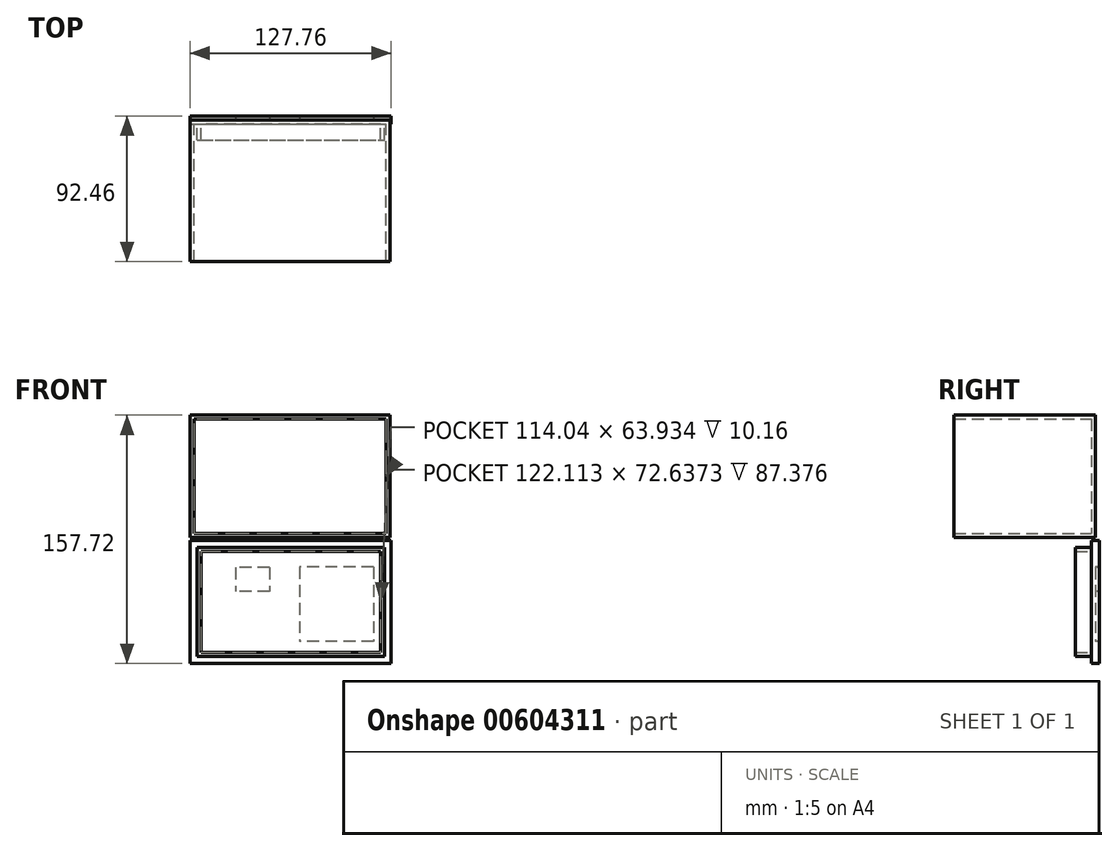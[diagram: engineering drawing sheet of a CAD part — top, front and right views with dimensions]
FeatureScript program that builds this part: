
annotation { "Feature Type Name" : "Feature", "Feature Type Description" : "" }
export const myFeature = defineFeature(function(context is Context, id is Id, definition is map)
    precondition{}
    {
        {
            var Q0;
            Q0=qCreatedBy(makeId("Front.planeOp"),FACE);
            var sketch = newSketch(context, id + "F0", { "sketchPlane" : qUnion([Q0])});
            skLineSegment(sketch, "E0.bottom", {"start": v(-147.35, 70.95) * mm, "end": v(-20.16, 70.95) * mm});
            skLineSegment(sketch, "E0.top", {"start": v(-147.35, -6.76) * mm, "end": v(-20.16, -6.76) * mm});
            skLineSegment(sketch, "E0.left", {"start": v(-147.35, 70.95) * mm, "end": v(-147.35, -6.76) * mm});
            skLineSegment(sketch, "E0.right", {"start": v(-20.16, 70.95) * mm, "end": v(-20.16, -6.76) * mm});
            skSolve(sketch);
        }
        {
            var Q0;
            Q0=makeQuery(id+"F0.imprint","IMPRINT",FACE,{"disambiguationData":[TD([[makeQuery(id+"F0.imprint","IMPRINT",EDGE,{"derivedFrom":sQuery(id+"F0.wireOp",EDGE,"E0.bottom")}),-1.0]])]});
            extrude(context, id + "F1", {"entities" : qUnion([Q0]), "depth" : 89.92 * mm, "offsetDistance" : 25.4 * mm});
        }
        {
            var Q0;
            Q0=makeQuery(id+"F1.opExtrude","CAP_FACE",FACE,{"disambiguationData":[OSD([sQuery(id+"F0.wireOp",EDGE,"E0.bottom"),sQuery(id+"F0.wireOp",EDGE,"E0.top"),sQuery(id+"F0.wireOp",EDGE,"E0.left"),sQuery(id+"F0.wireOp",EDGE,"E0.right")])],"isStart":false});
            shell(context, id + "F2", {"entities" : qUnion([Q0]), "thickness" : 2.54 * mm});
        }
        {
            var Q0;
            Q0=qCreatedBy(makeId("Front.planeOp"),FACE);
            var sketch = newSketch(context, id + "F3", { "sketchPlane" : qUnion([Q0])});
            skLineSegment(sketch, "E1.bottom", {"start": v(-147.14, -8.8) * mm, "end": v(-19.6, -8.8) * mm});
            skLineSegment(sketch, "E1.top", {"start": v(-147.14, -86.77) * mm, "end": v(-19.6, -86.77) * mm});
            skLineSegment(sketch, "E1.left", {"start": v(-147.14, -8.8) * mm, "end": v(-147.14, -86.77) * mm});
            skLineSegment(sketch, "E1.right", {"start": v(-19.6, -8.8) * mm, "end": v(-19.6, -86.77) * mm});
            skSolve(sketch);
        }
        {
            var Q0;
            Q0=makeQuery(id+"F3.imprint","IMPRINT",FACE,{"disambiguationData":[TD([[makeQuery(id+"F3.imprint","IMPRINT",EDGE,{"derivedFrom":sQuery(id+"F3.wireOp",EDGE,"E1.bottom")}),-1.0]])]});
            extrude(context, id + "F4", {"entities" : qUnion([Q0]), "depth" : 2.54 * mm, "offsetDistance" : 25.4 * mm});
        }
        {
            var Q0;
            Q0=makeQuery(id+"F4.opExtrude","CAP_FACE",FACE,{"disambiguationData":[OSD([sQuery(id+"F3.wireOp",EDGE,"E1.bottom"),sQuery(id+"F3.wireOp",EDGE,"E1.top"),sQuery(id+"F3.wireOp",EDGE,"E1.left"),sQuery(id+"F3.wireOp",EDGE,"E1.right")])],"isStart":false});
            var sketch = newSketch(context, id + "F5", { "sketchPlane" : qUnion([Q0])});
            skLineSegment(sketch, "E2.bottom", {"start": v(-142.77, -13.16) * mm, "end": v(-23.65, -13.16) * mm});
            skLineSegment(sketch, "E2.top", {"start": v(-142.77, -82.18) * mm, "end": v(-23.65, -82.18) * mm});
            skLineSegment(sketch, "E2.left", {"start": v(-142.77, -13.16) * mm, "end": v(-142.77, -82.18) * mm});
            skLineSegment(sketch, "E2.right", {"start": v(-23.65, -13.16) * mm, "end": v(-23.65, -82.18) * mm});
            skSolve(sketch);
        }
        {
            var Q0;
            Q0=makeQuery(id+"F5.imprint","IMPRINT",FACE,{"disambiguationData":[TD([[makeQuery(id+"F5.imprint","IMPRINT",EDGE,{"derivedFrom":sQuery(id+"F5.wireOp",EDGE,"E2.bottom")}),-1.0]])]});
            extrude(context, id + "F6", {"entities" : qUnion([Q0]), "operationType" : NewBodyOperationType.ADD, "depth" : 10.16 * mm, "offsetDistance" : 25.4 * mm});
        }
        {
            var Q0;
            Q0=makeQuery(id+"F4.opExtrude","CAP_FACE",FACE,{"disambiguationData":[OSD([sQuery(id+"F3.wireOp",EDGE,"E1.bottom"),sQuery(id+"F3.wireOp",EDGE,"E1.top"),sQuery(id+"F3.wireOp",EDGE,"E1.left"),sQuery(id+"F3.wireOp",EDGE,"E1.right")])],"isStart":true});
            var sketch = newSketch(context, id + "F7", { "sketchPlane" : qUnion([Q0])});
            skLineSegment(sketch, "E3.bottom", {"start": v(30.85, -25.45) * mm, "end": v(77.8, -25.45) * mm});
            skLineSegment(sketch, "E3.top", {"start": v(30.85, -72.72) * mm, "end": v(77.8, -72.72) * mm});
            skLineSegment(sketch, "E3.left", {"start": v(30.85, -25.45) * mm, "end": v(30.85, -72.72) * mm});
            skLineSegment(sketch, "E3.right", {"start": v(77.8, -25.45) * mm, "end": v(77.8, -72.72) * mm});
            skSolve(sketch);
        }
        {
            var Q0;
            Q0=makeQuery(id+"F7.imprint","IMPRINT",FACE,{"disambiguationData":[TD([[makeQuery(id+"F7.imprint","IMPRINT",EDGE,{"derivedFrom":sQuery(id+"F7.wireOp",EDGE,"E3.bottom")}),1.0]])]});
            var sketch = newSketch(context, id + "F8", { "sketchPlane" : qUnion([Q0])});
            skLineSegment(sketch, "E4.bottom", {"start": v(96.86, -25.9) * mm, "end": v(118.5, -25.9) * mm});
            skLineSegment(sketch, "E4.top", {"start": v(96.86, -41.15) * mm, "end": v(118.5, -41.15) * mm});
            skLineSegment(sketch, "E4.left", {"start": v(96.86, -25.9) * mm, "end": v(96.86, -41.15) * mm});
            skLineSegment(sketch, "E4.right", {"start": v(118.5, -25.9) * mm, "end": v(118.5, -41.15) * mm});
            skSolve(sketch);
        }
        {
            var Q0;
            Q0=makeQuery(id+"F6.opExtrude","CAP_FACE",FACE,{"disambiguationData":[OSD([sQuery(id+"F5.wireOp",EDGE,"E2.bottom"),sQuery(id+"F5.wireOp",EDGE,"E2.top"),sQuery(id+"F5.wireOp",EDGE,"E2.left"),sQuery(id+"F5.wireOp",EDGE,"E2.right")])],"isStart":false});
            shell(context, id + "F9", {"entities" : qUnion([Q0]), "thickness" : 2.54 * mm});
        }
        {
            var Q0;
            Q0=makeQuery(id+"F8.imprint","IMPRINT",FACE,{"disambiguationData":[TD([[makeQuery(id+"F8.imprint","IMPRINT",EDGE,{"derivedFrom":sQuery(id+"F8.wireOp",EDGE,"E4.bottom")}),1.0]])]});
            extrude(context, id + "F10", {"entities" : qUnion([Q0]), "operationType" : NewBodyOperationType.ADD, "depth" : 2.54 * mm, "offsetDistance" : 25.4 * mm});
        }
    });
